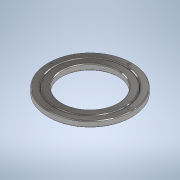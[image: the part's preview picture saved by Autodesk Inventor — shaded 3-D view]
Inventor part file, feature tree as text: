
AUTODESK INVENTOR PART (.ipt)
format: ipt  version: 2021 (Build 250183000, 183)  size: 169,984 bytes
history: native  units: mm
features: extrude x2, chamfer x2, sketch x2
ambient origin geometry x8: Origin, YZ Plane, XZ Plane, XY Plane, X Axis, Y Axis, Z Axis, Center Point
bodies: Solid1 (feature_tree)
feature tree (6):
  extrude  "Extrusion1"  Depth=100.0mm
  chamfer  "Chamfer1"  Distance=101.0mm
  chamfer  "Chamfer2"  Distance=8.5mm
  extrude  "Extrusion2"  Depth=8.5mm TaperAngle=45.0deg
  sketch  "Sketch1"  dims[d0=79.8mm d1=100.0mm]
  sketch  "Sketch2"  dims[d2=120.0mm d3=101.0mm d4=8.5mm d5=0.0mm d6=1.0mm d7=2.0mm d8=45.0deg d9=1.0mm d10=2.0mm d11=45.0deg d12=3.2mm d13=3.2mm d14=3.2mm d15=3.2mm d16=77.782mm d17=77.782mm d18=77.782mm d19=77.782mm d20=0.0mm d21=0.0mm d22=0.0mm d23=8.5mm d24=0.0mm d25=55.0mm]
